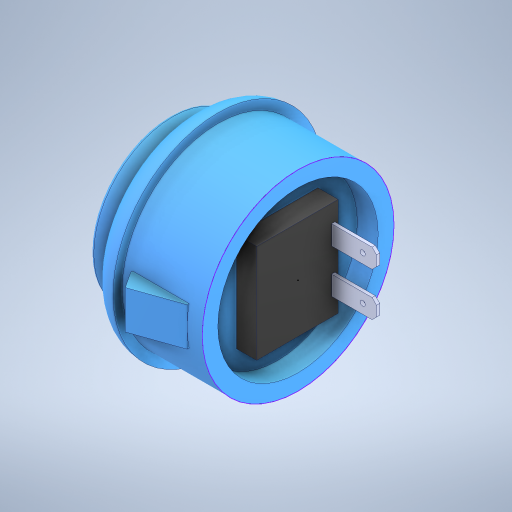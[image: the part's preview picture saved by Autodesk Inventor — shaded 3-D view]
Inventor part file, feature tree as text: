
AUTODESK INVENTOR PART (.ipt)
format: ipt  version: 2023.4 (Build 274418000, 418)  size: 366,592 bytes
history: native  units: in
note: dims shown in document units (in); Inventor stores cm internally (conversion verified against a paired STEP export)
features: sketch x1, fillet x1
ambient origin geometry x8: Origin, YZ Plane, XZ Plane, XY Plane, X Axis, Y Axis, Z Axis, Center Point
bodies: Solid1 (feature_tree)
feature tree (2):
  sketch  "Sketch1"
  fillet  "Fillet1"  [1 undecoded]
note: 1 required parameter value undecoded (feature->parameter linkage not recoverable at this tier; creation-order binding heuristic only, values carry confidence <= 0.55)
